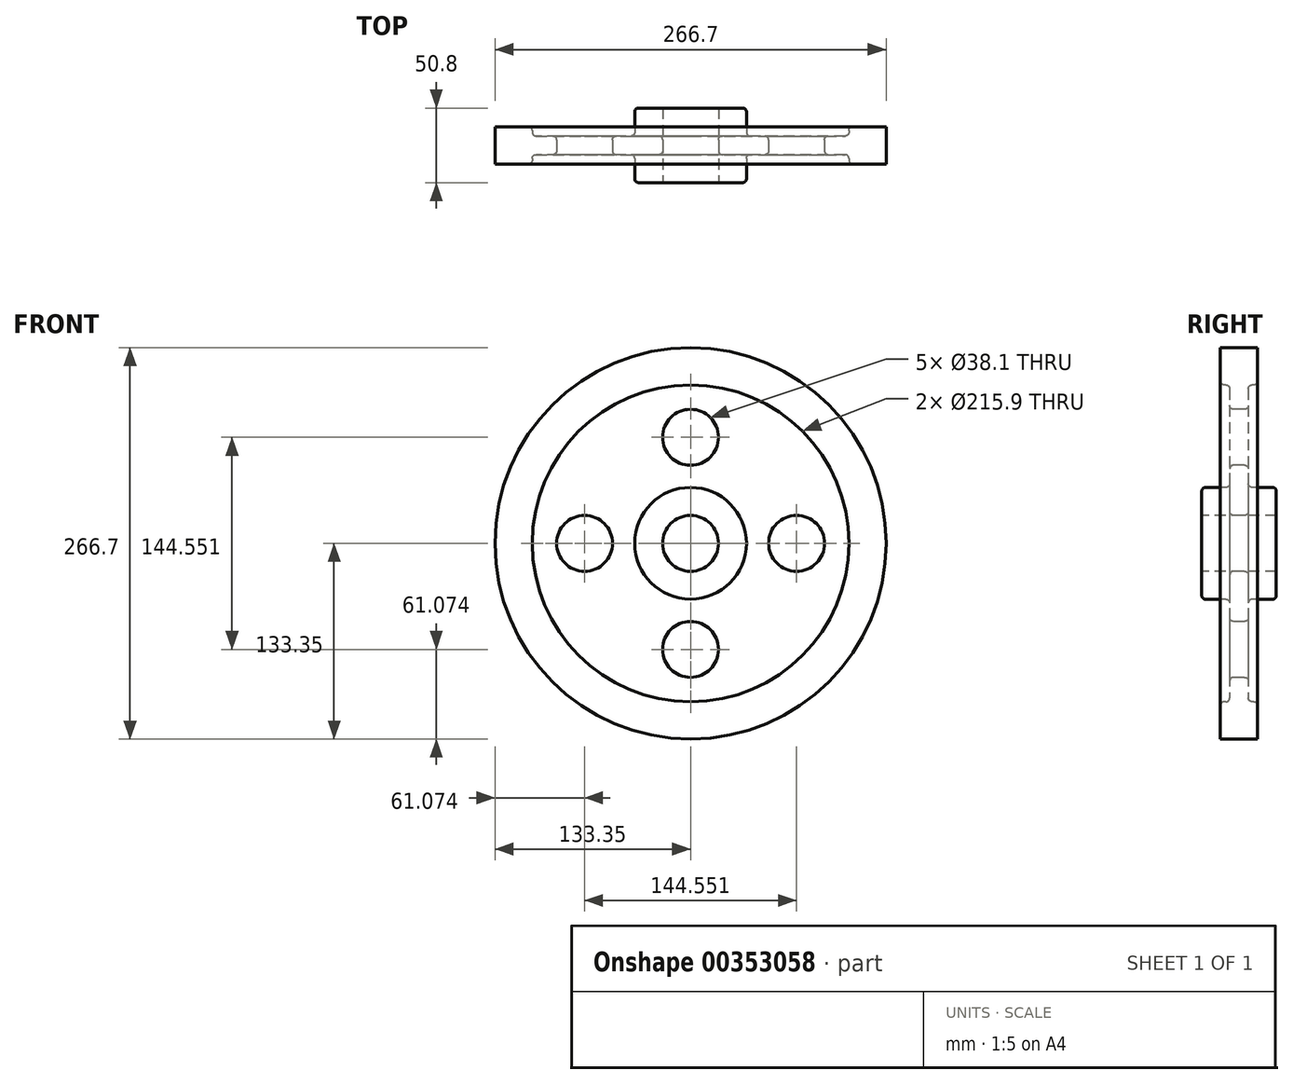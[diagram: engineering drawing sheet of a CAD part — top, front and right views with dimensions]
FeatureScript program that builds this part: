
annotation { "Feature Type Name" : "Feature", "Feature Type Description" : "" }
export const myFeature = defineFeature(function(context is Context, id is Id, definition is map)
    precondition{}
    {
        {
            var Q0;
            Q0=qCreatedBy(makeId("Right.planeOp"),FACE);
            var sketch = newSketch(context, id + "F0", { "sketchPlane" : qUnion([Q0])});
            skLineSegment(sketch, "E0", {"start": v(0, 0) * mm, "end": v(76.2, 0) * mm, "construction": true});
            skLineSegment(sketch, "E1.0", {"start": v(6.35, 38.1) * mm, "end": v(25.4, 38.1) * mm});
            skLineSegment(sketch, "E2.0", {"start": v(6.35, 107.95) * mm, "end": v(12.7, 107.95) * mm});
            skLineSegment(sketch, "E3.0", {"start": v(0, 133.35) * mm, "end": v(12.7, 133.35) * mm});
            skLineSegment(sketch, "E4", {"start": v(0, 0) * mm, "end": v(-7.33, 0) * mm, "construction": true});
            skLineSegment(sketch, "E5.0", {"start": v(6.35, 107.95) * mm, "end": v(6.35, 38.1) * mm});
            skLineSegment(sketch, "E6", {"start": v(153.63, 78.34) * mm, "end": v(156.3, 84.54) * mm});
            skLineSegment(sketch, "E7.0", {"start": v(25.4, 38.1) * mm, "end": v(25.4, 19.05) * mm});
            skLineSegment(sketch, "E8.0", {"start": v(12.7, 133.35) * mm, "end": v(12.7, 107.95) * mm});
            skLineSegment(sketch, "E9", {"start": v(25.4, 19.05) * mm, "end": v(0, 19.05) * mm});
            skLineSegment(sketch, "E10.MirrorCS", {"start": v(-6.35, 107.95) * mm, "end": v(-6.35, 38.1) * mm});
            skLineSegment(sketch, "E11.MirrorCS", {"start": v(-12.7, 133.35) * mm, "end": v(-12.7, 107.95) * mm});
            skLineSegment(sketch, "E12.MirrorCS", {"start": v(-6.35, 38.1) * mm, "end": v(-25.4, 38.1) * mm});
            skLineSegment(sketch, "E13.MirrorCS", {"start": v(-25.4, 38.1) * mm, "end": v(-25.4, 19.05) * mm});
            skLineSegment(sketch, "E14.MirrorCS", {"start": v(-25.4, 19.05) * mm, "end": v(0, 19.05) * mm});
            skLineSegment(sketch, "E15.MirrorCS", {"start": v(0, 133.35) * mm, "end": v(-12.7, 133.35) * mm});
            skLineSegment(sketch, "E16.MirrorCS", {"start": v(0, 0) * mm, "end": v(-76.2, 0) * mm, "construction": true});
            skLineSegment(sketch, "E17.MirrorCS", {"start": v(-6.35, 107.95) * mm, "end": v(-12.7, 107.95) * mm});
            skSolve(sketch);
        }
        {
            var Q0;
            Q0=makeQuery(id+"F0.imprint","IMPRINT",FACE,{"disambiguationData":[TD([[makeQuery(id+"F0.imprint","IMPRINT",EDGE,{"derivedFrom":sQuery(id+"F0.wireOp",EDGE,"E1.0")}),-1.0]])]});
            var Q1;
            Q1=sQuery(id+"F0.wireOp",EDGE,"E0");
            revolve(context, id + "F1", {"entities" : qUnion([Q0]), "axis" : qUnion([Q1]), "revolveType" : RevolveType.FULL});
        }
        {
            var Q0;
            Q0=makeQuery(id+"F1.opRevolve","SWEPT_FACE",FACE,{"disambiguationData":[OSD([sQuery(id+"F0.wireOp",EDGE,"E13.MirrorCS")])]});
            var sketch = newSketch(context, id + "F2", { "sketchPlane" : qUnion([Q0])});
            skLineSegment(sketch, "E18", {"start": v(0, 0) * mm, "end": v(0, 72.28) * mm});
            skCircle(sketch, "E19", {"center": v(0, 72.28) * mm, "radius": 19.05 * mm});
            skCircle(sketch, "E20.1.0", {"center": v(-72.28, 0) * mm, "radius": 19.05 * mm});
            skCircle(sketch, "E20.2.0", {"center": v(0, -72.28) * mm, "radius": 19.05 * mm});
            skPoint(sketch, "E20.center", {"position": v(0, 0) * mm});
            skCircle(sketch, "E21.1.3.0", {"center": v(72.28, 0) * mm, "radius": 19.05 * mm});
            skSolve(sketch);
        }
        {
            var Q0;
            Q0 = qSketchRegion(id + "F2", true);
            extrude(context, id + "F3", {"entities" : qUnion([Q0]), "operationType" : NewBodyOperationType.REMOVE, "oppositeDirection" : true, "depth" : 25.4 * mm});
        }
        {
            var Q0;
            Q0=makeQuery(id+"F3.boolean.opBoolean","COPY",FACE,{"derivedFrom":makeQuery(id+"F3.opExtrude","CAP_FACE",FACE,{"disambiguationData":[OSD([sQuery(id+"F2.wireOp",EDGE,"E20.1.0")])],"isStart":false})});
            var Q1;
            Q1=makeQuery(id+"F3.boolean.opBoolean","COPY",FACE,{"derivedFrom":makeQuery(id+"F3.opExtrude","CAP_FACE",FACE,{"disambiguationData":[OSD([sQuery(id+"F2.wireOp",EDGE,"E21.1.3.0")])],"isStart":false})});
            var Q2;
            Q2=makeQuery(id+"F3.boolean.opBoolean","COPY",FACE,{"derivedFrom":makeQuery(id+"F3.opExtrude","CAP_FACE",FACE,{"disambiguationData":[OSD([sQuery(id+"F2.wireOp",EDGE,"E20.2.0")])],"isStart":false})});
            var Q3;
            Q3=makeQuery(id+"F3.boolean.opBoolean","COPY",FACE,{"derivedFrom":makeQuery(id+"F3.opExtrude","CAP_FACE",FACE,{"disambiguationData":[OSD([sQuery(id+"F2.wireOp",EDGE,"E19")])],"isStart":false})});
            extrude(context, id + "F4", {"entities" : qUnion([Q0, Q1, Q2, Q3]), "operationType" : NewBodyOperationType.REMOVE, "oppositeDirection" : true, "depth" : 25.4 * mm});
        }
        {
            var Q0;
            Q0=makeQuery(id+"F1.opRevolve","SWEPT_EDGE",EDGE,{"disambiguationData":[OSD([sQuery(id+"F0.wireOp",EDGE,"E10.MirrorCS"),sQuery(id+"F0.wireOp",EDGE,"E17.MirrorCS")])]});
            var Q1;
            Q1=makeQuery(id+"F1.opRevolve","SWEPT_EDGE",EDGE,{"disambiguationData":[OSD([sQuery(id+"F0.wireOp",EDGE,"E1.0"),sQuery(id+"F0.wireOp",EDGE,"E7.0")])]});
            var Q2;
            Q2=makeQuery(id+"F1.opRevolve","SWEPT_EDGE",EDGE,{"disambiguationData":[OSD([sQuery(id+"F0.wireOp",EDGE,"E1.0"),sQuery(id+"F0.wireOp",EDGE,"E5.0")])]});
            var Q3;
            Q3=makeQuery(id+"F1.opRevolve","SWEPT_FACE",FACE,{"disambiguationData":[OSD([sQuery(id+"F0.wireOp",EDGE,"E5.0")])]});
            var Q4;
            Q4=makeQuery(id+"F1.opRevolve","SWEPT_EDGE",EDGE,{"disambiguationData":[OSD([sQuery(id+"F0.wireOp",EDGE,"E2.0"),sQuery(id+"F0.wireOp",EDGE,"E5.0")])]});
            var Q5;
            Q5=makeQuery(id+"F1.opRevolve","SWEPT_EDGE",EDGE,{"disambiguationData":[OSD([sQuery(id+"F0.wireOp",EDGE,"E2.0"),sQuery(id+"F0.wireOp",EDGE,"E8.0")])]});
            var Q6;
            Q6=makeQuery(id+"F1.opRevolve","SWEPT_FACE",FACE,{"disambiguationData":[OSD([sQuery(id+"F0.wireOp",EDGE,"E10.MirrorCS")])]});
            var Q7;
            Q7=makeQuery(id+"F1.opRevolve","SWEPT_EDGE",EDGE,{"disambiguationData":[OSD([sQuery(id+"F0.wireOp",EDGE,"E12.MirrorCS"),sQuery(id+"F0.wireOp",EDGE,"E13.MirrorCS")])]});
            var Q8;
            Q8=makeQuery(id+"F1.opRevolve","SWEPT_EDGE",EDGE,{"disambiguationData":[OSD([sQuery(id+"F0.wireOp",EDGE,"E11.MirrorCS"),sQuery(id+"F0.wireOp",EDGE,"E17.MirrorCS")])]});
            fillet(context, id + "F5", {"entities" : qUnion([Q0, Q1, Q2, Q3, Q4, Q5, Q6, Q7, Q8]), "radius" : 2.54 * mm, "tangentPropagation" : true, "allowEdgeOverflow" : false});
        }
    });
